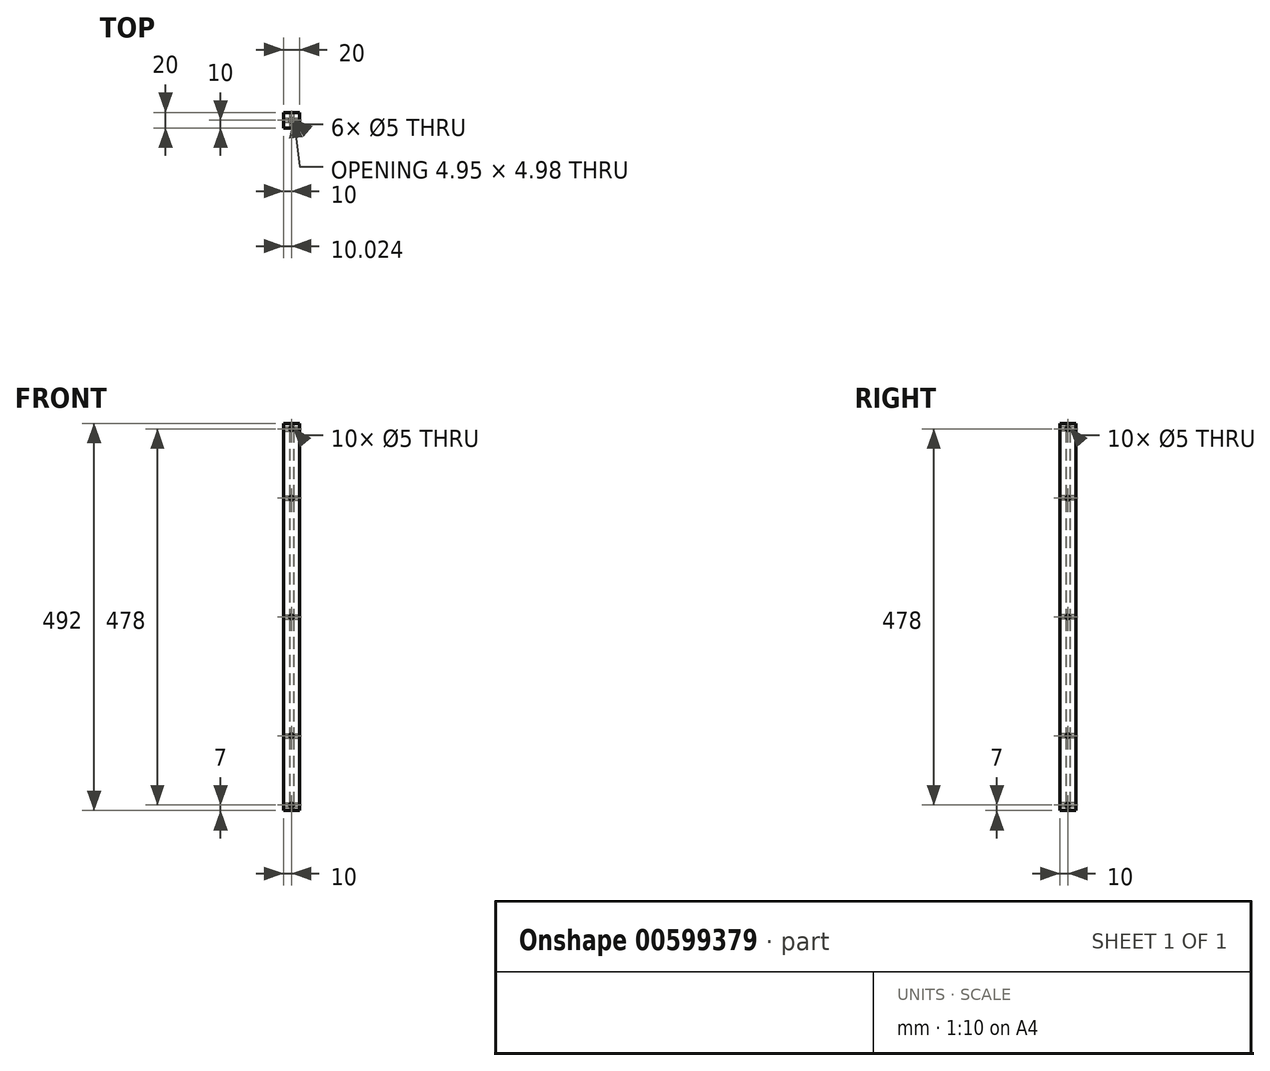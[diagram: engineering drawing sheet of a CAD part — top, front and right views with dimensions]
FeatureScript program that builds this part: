
annotation { "Feature Type Name" : "Feature", "Feature Type Description" : "" }
export const myFeature = defineFeature(function(context is Context, id is Id, definition is map)
    precondition{}
    {
        {
            var Q0;
            Q0=qCreatedBy(makeId("Top.planeOp"),FACE);
            var sketch = newSketch(context, id + "F0", { "sketchPlane" : qUnion([Q0])});
            skLineSegment(sketch, "E0.bottom", {"start": v(-10, 10) * mm, "end": v(10, 10) * mm});
            skLineSegment(sketch, "E0.top", {"start": v(-10, -10) * mm, "end": v(10, -10) * mm});
            skLineSegment(sketch, "E0.left", {"start": v(-10, 10) * mm, "end": v(-10, -10) * mm});
            skLineSegment(sketch, "E0.right", {"start": v(10, 10) * mm, "end": v(10, -10) * mm});
            skCircle(sketch, "E1", {"center": v(0, 0) * mm, "radius": 2.5 * mm});
            skSolve(sketch);
        }
        {
            var Q0;
            Q0=qSketchRegion(id+"F0",true);
            extrude(context, id + "F1", {"entities" : qUnion([Q0]), "depth" : 492 * mm, "offsetDistance" : 25 * mm});
        }
        {
            var Q0;
            Q0=makeQuery(id+"F1.opExtrude","SWEPT_FACE",FACE,{"disambiguationData":[OSD([sQuery(id+"F0.wireOp",EDGE,"E0.right")])]});
            var sketch = newSketch(context, id + "F2", { "sketchPlane" : qUnion([Q0])});
            skCircle(sketch, "E2", {"center": v(0, 7) * mm, "radius": 2.5 * mm});
            skCircle(sketch, "E3", {"center": v(0, 485) * mm, "radius": 2.5 * mm});
            skCircle(sketch, "E4", {"center": v(0, 246) * mm, "radius": 2.5 * mm});
            skPoint(sketch, "E4.centerSnap0", {"position": v(-10, 246) * mm});
            skCircle(sketch, "E5", {"center": v(0, 95.13) * mm, "radius": 2.5 * mm});
            skCircle(sketch, "E6", {"center": v(0, 396.87) * mm, "radius": 2.5 * mm});
            skSolve(sketch);
        }
        {
            var Q0;
            Q0=qSketchRegion(id+"F2",true);
            extrude(context, id + "F3", {"entities" : qUnion([Q0]), "operationType" : NewBodyOperationType.REMOVE, "endBound" : BoundingType.THROUGH_ALL, "oppositeDirection" : true, "depth" : 25 * mm});
        }
        {
            var Q0;
            Q0=makeQuery(id+"F1.opExtrude","SWEPT_FACE",FACE,{"disambiguationData":[OSD([sQuery(id+"F0.wireOp",EDGE,"E0.top")])]});
            var sketch = newSketch(context, id + "F4", { "sketchPlane" : qUnion([Q0])});
            skCircle(sketch, "E7", {"center": v(0, 246) * mm, "radius": 2.5 * mm});
            skPoint(sketch, "E7.centerSnap0", {"position": v(-10, 246) * mm});
            skCircle(sketch, "E8", {"center": v(0, 485) * mm, "radius": 2.5 * mm});
            skCircle(sketch, "E9", {"center": v(0, 7) * mm, "radius": 2.5 * mm});
            skCircle(sketch, "E10", {"center": v(0, 95.13) * mm, "radius": 2.5 * mm});
            skCircle(sketch, "E11", {"center": v(0, 396.87) * mm, "radius": 2.5 * mm});
            skSolve(sketch);
        }
        {
            var Q0;
            Q0=qSketchRegion(id+"F4",true);
            extrude(context, id + "F5", {"entities" : qUnion([Q0]), "operationType" : NewBodyOperationType.REMOVE, "endBound" : BoundingType.THROUGH_ALL, "oppositeDirection" : true, "depth" : 25 * mm});
        }
    });
